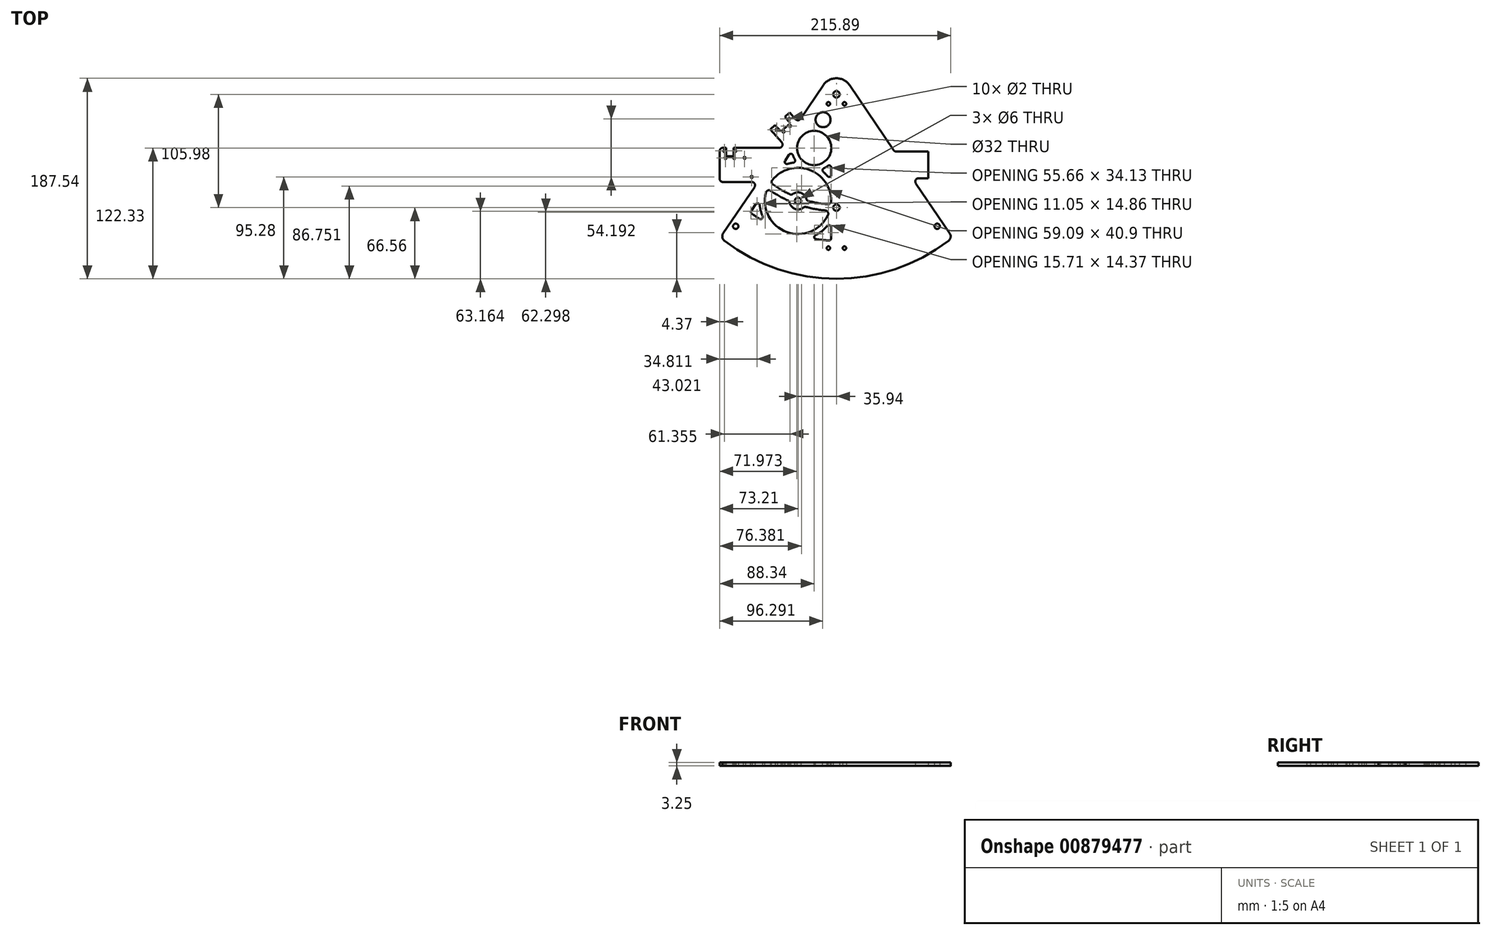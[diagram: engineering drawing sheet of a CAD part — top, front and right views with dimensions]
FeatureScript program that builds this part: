
annotation { "Feature Type Name" : "Feature", "Feature Type Description" : "" }
export const myFeature = defineFeature(function(context is Context, id is Id, definition is map)
    precondition{}
    {
        {
            var Q0;
            Q0=qCreatedBy(makeId("Top.planeOp"),FACE);
            var sketch = newSketch(context, id + "F0", { "sketchPlane" : qUnion([Q0])});
            skLineSegment(sketch, "E0", {"start": v(-12.44, 8.39) * mm, "end": v(-33.57, -22.95) * mm});
            skLineSegment(sketch, "E1", {"start": v(12.44, 8.39) * mm, "end": v(53.3, -52.2) * mm});
            skArc(sketch, "E2", {"start": v(-104.78, -136.9) * mm, "mid": v(0, -172.54) * mm, "end": v(104.78, -136.9) * mm});
            skPoint(sketch, "E3.visualSharp", {"position": v(0, 26.82) * mm});
            skArc(sketch, "E3.filletArc", {"start": v(12.44, 8.39) * mm, "mid": v(0, 15) * mm, "end": v(-12.44, 8.39) * mm});
            skPoint(sketch, "E4.visualSharp", {"position": v(108.47, -134) * mm});
            skArc(sketch, "E4.filletArc", {"start": v(104.78, -136.9) * mm, "mid": v(106.67, -133.75) * mm, "end": v(105.88, -130.15) * mm});
            skPoint(sketch, "E5.visualSharp", {"position": v(-108.47, -134) * mm});
            skArc(sketch, "E5.filletArc", {"start": v(-105.88, -130.15) * mm, "mid": v(-106.67, -133.75) * mm, "end": v(-104.78, -136.9) * mm});
            skLineSegment(sketch, "E6", {"start": v(-114.15, -172.54) * mm, "end": v(114.15, -172.54) * mm, "construction": true});
            skLineSegment(sketch, "E7", {"start": v(-114.15, 15) * mm, "end": v(114.15, 15) * mm, "construction": true});
            skPoint(sketch, "E8", {"position": v(-94.16, -123.45) * mm});
            skPoint(sketch, "E9", {"position": v(94.16, -123.45) * mm});
            skPoint(sketch, "E10", {"position": v(-7.5, -8.89) * mm});
            skPoint(sketch, "E11", {"position": v(7.5, -8.89) * mm});
            skLineSegment(sketch, "E12.bottom", {"start": v(55.79, -53.52) * mm, "end": v(85.7, -53.52) * mm});
            skLineSegment(sketch, "E12.top", {"start": v(76.7, -78.52) * mm, "end": v(85.7, -78.52) * mm});
            skLineSegment(sketch, "E12.right", {"start": v(85.7, -53.52) * mm, "end": v(85.7, -78.52) * mm});
            skLineSegment(sketch, "E13.trimOffspring", {"start": v(74.21, -83.2) * mm, "end": v(105.88, -130.15) * mm});
            skLineSegment(sketch, "E14.bottom", {"start": v(-53.43, -50.02) * mm, "end": v(-96.15, -50.02) * mm});
            skLineSegment(sketch, "E14.top", {"start": v(-79.06, -82.02) * mm, "end": v(-106.15, -82.02) * mm});
            skLineSegment(sketch, "E14.right", {"start": v(-109.15, -53.02) * mm, "end": v(-109.15, -79.02) * mm});
            skLineSegment(sketch, "E15.trimOffspring", {"start": v(-76.57, -86.7) * mm, "end": v(-105.88, -130.15) * mm});
            skLineSegment(sketch, "E16.top", {"start": v(-103.15, -58.02) * mm, "end": v(-96.15, -58.02) * mm});
            skLineSegment(sketch, "E16.left", {"start": v(-103.15, -50.02) * mm, "end": v(-103.15, -58.02) * mm});
            skLineSegment(sketch, "E16.right", {"start": v(-96.15, -50.02) * mm, "end": v(-96.15, -58.02) * mm});
            skLineSegment(sketch, "E17", {"start": v(-51.16, -45.05) * mm, "end": v(-61.82, -32.8) * mm});
            skLineSegment(sketch, "E18", {"start": v(-61.82, -32.8) * mm, "end": v(-57.3, -28.86) * mm});
            skLineSegment(sketch, "E19", {"start": v(-57.3, -28.86) * mm, "end": v(-52.04, -34.9) * mm});
            skLineSegment(sketch, "E20", {"start": v(-52.04, -34.9) * mm, "end": v(-42.99, -27.02) * mm});
            skLineSegment(sketch, "E21", {"start": v(-42.99, -27.02) * mm, "end": v(-48.23, -20.99) * mm});
            skLineSegment(sketch, "E22", {"start": v(-48.23, -20.99) * mm, "end": v(-43.7, -17.05) * mm});
            skLineSegment(sketch, "E23", {"start": v(-43.7, -17.05) * mm, "end": v(-38.32, -23.24) * mm});
            skLineSegment(sketch, "E24.trimOffspring", {"start": v(-103.15, -50.02) * mm, "end": v(-106.15, -50.02) * mm});
            skLineSegment(sketch, "E25", {"start": v(-114.15, 15) * mm, "end": v(-114.15, -172.54) * mm, "construction": true});
            skLineSegment(sketch, "E26", {"start": v(114.15, -172.54) * mm, "end": v(114.15, 15) * mm, "construction": true});
            skArc(sketch, "E27.filletArc", {"start": v(-53.43, -50.02) * mm, "mid": v(-50.7, -48.26) * mm, "end": v(-51.16, -45.05) * mm});
            skLineSegment(sketch, "E28", {"start": v(-48.23, -20.99) * mm, "end": v(-32.25, -20.99) * mm, "construction": true});
            skPoint(sketch, "E29.visualSharp", {"position": v(-35.76, -26.2) * mm});
            skArc(sketch, "E29.filletArc", {"start": v(-38.32, -23.24) * mm, "mid": v(-35.88, -24.27) * mm, "end": v(-33.57, -22.95) * mm});
            skPoint(sketch, "E30.visualSharp", {"position": v(-73.42, -82.02) * mm});
            skArc(sketch, "E30.filletArc", {"start": v(-76.57, -86.7) * mm, "mid": v(-76.4, -83.61) * mm, "end": v(-79.06, -82.02) * mm});
            skPoint(sketch, "E31.visualSharp", {"position": v(-109.15, -50.02) * mm});
            skArc(sketch, "E31.filletArc", {"start": v(-106.15, -50.02) * mm, "mid": v(-108.27, -50.9) * mm, "end": v(-109.15, -53.02) * mm});
            skPoint(sketch, "E32.visualSharp", {"position": v(-109.15, -82.02) * mm});
            skArc(sketch, "E32.filletArc", {"start": v(-109.15, -79.02) * mm, "mid": v(-108.27, -81.14) * mm, "end": v(-106.15, -82.02) * mm});
            skPoint(sketch, "E33.visualSharp", {"position": v(71.06, -78.52) * mm});
            skArc(sketch, "E33.filletArc", {"start": v(76.7, -78.52) * mm, "mid": v(74.05, -80.11) * mm, "end": v(74.21, -83.2) * mm});
            skPoint(sketch, "E34.visualSharp", {"position": v(54.2, -53.52) * mm});
            skArc(sketch, "E34.filletArc", {"start": v(53.3, -52.2) * mm, "mid": v(54.38, -53.17) * mm, "end": v(55.79, -53.52) * mm});
            skPoint(sketch, "E35", {"position": v(-7.5, -143.86) * mm});
            skPoint(sketch, "E36", {"position": v(7.5, -143.86) * mm});
            skPoint(sketch, "E37", {"position": v(0, -105.98) * mm});
            skSolve(sketch);
        }
        {
            var Q0;
            Q0=makeQuery(id+"F0.imprint","IMPRINT",FACE,{"disambiguationData":[TD([[makeQuery(id+"F0.imprint","IMPRINT",EDGE,{"derivedFrom":sQuery(id+"F0.wireOp",EDGE,"E0")}),1.0]])]});
            extrude(context, id + "F1", {"entities" : qUnion([Q0]), "depth" : 3.25 * mm, "offsetDistance" : 25 * mm});
        }
        {
            var Q0;
            Q0=sQuery(id+"F0.wireOp",VERTEX,"E9");
            var Q1;
            Q1=sQuery(id+"F0.wireOp",VERTEX,"E8");
            var Q2;
            Q2=makeQuery(id+"F1.opExtrude","SWEPT_BODY",BODY,{"disambiguationData":[OSD([sQuery(id+"F0.wireOp",EDGE,"E0"),sQuery(id+"F0.wireOp",EDGE,"E1"),sQuery(id+"F0.wireOp",EDGE,"E2"),sQuery(id+"F0.wireOp",EDGE,"E3.filletArc"),sQuery(id+"F0.wireOp",EDGE,"E4.filletArc"),sQuery(id+"F0.wireOp",EDGE,"E5.filletArc"),sQuery(id+"F0.wireOp",EDGE,"E12.bottom"),sQuery(id+"F0.wireOp",EDGE,"E12.top"),sQuery(id+"F0.wireOp",EDGE,"E12.right"),sQuery(id+"F0.wireOp",EDGE,"E13.trimOffspring"),sQuery(id+"F0.wireOp",EDGE,"E14.bottom"),sQuery(id+"F0.wireOp",EDGE,"E14.top"),sQuery(id+"F0.wireOp",EDGE,"E14.right"),sQuery(id+"F0.wireOp",EDGE,"E15.trimOffspring"),sQuery(id+"F0.wireOp",EDGE,"E16.top"),sQuery(id+"F0.wireOp",EDGE,"E16.left"),sQuery(id+"F0.wireOp",EDGE,"E16.right"),sQuery(id+"F0.wireOp",EDGE,"E17"),sQuery(id+"F0.wireOp",EDGE,"E18"),sQuery(id+"F0.wireOp",EDGE,"E19"),sQuery(id+"F0.wireOp",EDGE,"E20"),sQuery(id+"F0.wireOp",EDGE,"E21"),sQuery(id+"F0.wireOp",EDGE,"E22"),sQuery(id+"F0.wireOp",EDGE,"E23"),sQuery(id+"F0.wireOp",EDGE,"E24.trimOffspring"),sQuery(id+"F0.wireOp",EDGE,"E27.filletArc"),sQuery(id+"F0.wireOp",EDGE,"E29.filletArc"),sQuery(id+"F0.wireOp",EDGE,"E30.filletArc"),sQuery(id+"F0.wireOp",EDGE,"E31.filletArc"),sQuery(id+"F0.wireOp",EDGE,"E32.filletArc"),sQuery(id+"F0.wireOp",EDGE,"E33.filletArc"),sQuery(id+"F0.wireOp",EDGE,"E34.filletArc")])]});
            hole(context, id + "F2", {"style" : HoleStyle.SIMPLE, "endStyle" : HoleEndStyle.THROUGH, "oppositeDirection" : true, "standardTappedOrClearance" : lookupTablePath({ "standard" : "ISO", "engagement" : "75%", "pitch" : "1 mm", "size" : "M6", "type" : "Tapped" }), "standardBlindInLast" : lookupTablePath({ "standard" : "ISO", "engagement" : "75%", "pitch" : "1 mm", "size" : "M6", "type" : "Tapped" }), "holeDiameter" : 5 * mm, "majorDiameter" : 6 * mm, "showTappedDepth" : true, "isTappedThrough" : true, "tappedDepth" : 12 * mm, "tapClearance" : 3, "startFromSketch" : true, "locations" : qUnion([Q0, Q1]), "scope" : qUnion([Q2])});
        }
        {
            var Q0;
            Q0=sQuery(id+"F0.wireOp",VERTEX,"E10");
            var Q1;
            Q1=sQuery(id+"F0.wireOp",VERTEX,"E11");
            var Q2;
            Q2=sQuery(id+"F0.wireOp",VERTEX,"E35");
            var Q3;
            Q3=sQuery(id+"F0.wireOp",VERTEX,"E36");
            var Q4;
            Q4=makeQuery(id+"F1.opExtrude","SWEPT_BODY",BODY,{"disambiguationData":[OSD([sQuery(id+"F0.wireOp",EDGE,"E0"),sQuery(id+"F0.wireOp",EDGE,"E1"),sQuery(id+"F0.wireOp",EDGE,"E2"),sQuery(id+"F0.wireOp",EDGE,"E3.filletArc"),sQuery(id+"F0.wireOp",EDGE,"E4.filletArc"),sQuery(id+"F0.wireOp",EDGE,"E5.filletArc"),sQuery(id+"F0.wireOp",EDGE,"E12.bottom"),sQuery(id+"F0.wireOp",EDGE,"E12.top"),sQuery(id+"F0.wireOp",EDGE,"E12.right"),sQuery(id+"F0.wireOp",EDGE,"E13.trimOffspring"),sQuery(id+"F0.wireOp",EDGE,"E14.bottom"),sQuery(id+"F0.wireOp",EDGE,"E14.top"),sQuery(id+"F0.wireOp",EDGE,"E14.right"),sQuery(id+"F0.wireOp",EDGE,"E15.trimOffspring"),sQuery(id+"F0.wireOp",EDGE,"E16.top"),sQuery(id+"F0.wireOp",EDGE,"E16.left"),sQuery(id+"F0.wireOp",EDGE,"E16.right"),sQuery(id+"F0.wireOp",EDGE,"E17"),sQuery(id+"F0.wireOp",EDGE,"E18"),sQuery(id+"F0.wireOp",EDGE,"E19"),sQuery(id+"F0.wireOp",EDGE,"E20"),sQuery(id+"F0.wireOp",EDGE,"E21"),sQuery(id+"F0.wireOp",EDGE,"E22"),sQuery(id+"F0.wireOp",EDGE,"E23"),sQuery(id+"F0.wireOp",EDGE,"E24.trimOffspring"),sQuery(id+"F0.wireOp",EDGE,"E27.filletArc"),sQuery(id+"F0.wireOp",EDGE,"E29.filletArc"),sQuery(id+"F0.wireOp",EDGE,"E30.filletArc"),sQuery(id+"F0.wireOp",EDGE,"E31.filletArc"),sQuery(id+"F0.wireOp",EDGE,"E32.filletArc"),sQuery(id+"F0.wireOp",EDGE,"E33.filletArc"),sQuery(id+"F0.wireOp",EDGE,"E34.filletArc")])]});
            hole(context, id + "F3", {"style" : HoleStyle.SIMPLE, "endStyle" : HoleEndStyle.THROUGH, "oppositeDirection" : true, "standardTappedOrClearance" : lookupTablePath({ "standard" : "ISO", "engagement" : "75%", "pitch" : "0.7 mm", "size" : "M4", "type" : "Tapped" }), "standardBlindInLast" : lookupTablePath({ "standard" : "ISO", "engagement" : "75%", "pitch" : "0.7 mm", "size" : "M4", "type" : "Tapped" }), "holeDiameter" : 3.3 * mm, "majorDiameter" : 4 * mm, "showTappedDepth" : true, "isTappedThrough" : true, "tappedDepth" : 12 * mm, "tapClearance" : 3, "startFromSketch" : true, "locations" : qUnion([Q0, Q1, Q2, Q3]), "scope" : qUnion([Q4])});
        }
        {
            var Q0;
            Q0=sQuery(id+"F0.wireOp",VERTEX,"E3.filletArc.center");
            var Q1;
            Q1=sQuery(id+"F0.wireOp",VERTEX,"E37");
            var Q2;
            Q2=makeQuery(id+"F1.opExtrude","SWEPT_BODY",BODY,{"disambiguationData":[OSD([sQuery(id+"F0.wireOp",EDGE,"E0"),sQuery(id+"F0.wireOp",EDGE,"E1"),sQuery(id+"F0.wireOp",EDGE,"E2"),sQuery(id+"F0.wireOp",EDGE,"E3.filletArc"),sQuery(id+"F0.wireOp",EDGE,"E4.filletArc"),sQuery(id+"F0.wireOp",EDGE,"E5.filletArc"),sQuery(id+"F0.wireOp",EDGE,"E12.bottom"),sQuery(id+"F0.wireOp",EDGE,"E12.top"),sQuery(id+"F0.wireOp",EDGE,"E12.right"),sQuery(id+"F0.wireOp",EDGE,"E13.trimOffspring"),sQuery(id+"F0.wireOp",EDGE,"E14.bottom"),sQuery(id+"F0.wireOp",EDGE,"E14.top"),sQuery(id+"F0.wireOp",EDGE,"E14.right"),sQuery(id+"F0.wireOp",EDGE,"E15.trimOffspring"),sQuery(id+"F0.wireOp",EDGE,"E16.top"),sQuery(id+"F0.wireOp",EDGE,"E16.left"),sQuery(id+"F0.wireOp",EDGE,"E16.right"),sQuery(id+"F0.wireOp",EDGE,"E17"),sQuery(id+"F0.wireOp",EDGE,"E18"),sQuery(id+"F0.wireOp",EDGE,"E19"),sQuery(id+"F0.wireOp",EDGE,"E20"),sQuery(id+"F0.wireOp",EDGE,"E21"),sQuery(id+"F0.wireOp",EDGE,"E22"),sQuery(id+"F0.wireOp",EDGE,"E23"),sQuery(id+"F0.wireOp",EDGE,"E24.trimOffspring"),sQuery(id+"F0.wireOp",EDGE,"E27.filletArc"),sQuery(id+"F0.wireOp",EDGE,"E29.filletArc"),sQuery(id+"F0.wireOp",EDGE,"E30.filletArc"),sQuery(id+"F0.wireOp",EDGE,"E31.filletArc"),sQuery(id+"F0.wireOp",EDGE,"E32.filletArc"),sQuery(id+"F0.wireOp",EDGE,"E33.filletArc"),sQuery(id+"F0.wireOp",EDGE,"E34.filletArc")])]});
            hole(context, id + "F4", {"style" : HoleStyle.SIMPLE, "endStyle" : HoleEndStyle.THROUGH, "oppositeDirection" : true, "standardTappedOrClearance" : lookupTablePath({ "standard" : "ISO", "size" : "6", "type" : "Drilled" }), "standardBlindInLast" : lookupTablePath({ "standard" : "ISO", "size" : "6", "type" : "Drilled" }), "holeDiameter" : 6 * mm, "majorDiameter" : 4 * mm, "isTappedThrough" : true, "tappedDepth" : 12 * mm, "tapClearance" : 3, "startFromSketch" : true, "locations" : qUnion([Q0, Q1]), "scope" : qUnion([Q2])});
        }
        {
            var Q0;
            Q0=makeQuery(id+"F1.opExtrude","CAP_FACE",FACE,{"disambiguationData":[OSD([sQuery(id+"F0.wireOp",EDGE,"E0"),sQuery(id+"F0.wireOp",EDGE,"E1"),sQuery(id+"F0.wireOp",EDGE,"E2"),sQuery(id+"F0.wireOp",EDGE,"E3.filletArc"),sQuery(id+"F0.wireOp",EDGE,"E4.filletArc"),sQuery(id+"F0.wireOp",EDGE,"E5.filletArc"),sQuery(id+"F0.wireOp",EDGE,"E12.bottom"),sQuery(id+"F0.wireOp",EDGE,"E12.top"),sQuery(id+"F0.wireOp",EDGE,"E12.right"),sQuery(id+"F0.wireOp",EDGE,"E13.trimOffspring"),sQuery(id+"F0.wireOp",EDGE,"E14.bottom"),sQuery(id+"F0.wireOp",EDGE,"E14.top"),sQuery(id+"F0.wireOp",EDGE,"E14.right"),sQuery(id+"F0.wireOp",EDGE,"E15.trimOffspring"),sQuery(id+"F0.wireOp",EDGE,"E16.top"),sQuery(id+"F0.wireOp",EDGE,"E16.left"),sQuery(id+"F0.wireOp",EDGE,"E16.right"),sQuery(id+"F0.wireOp",EDGE,"E17"),sQuery(id+"F0.wireOp",EDGE,"E18"),sQuery(id+"F0.wireOp",EDGE,"E19"),sQuery(id+"F0.wireOp",EDGE,"E20"),sQuery(id+"F0.wireOp",EDGE,"E21"),sQuery(id+"F0.wireOp",EDGE,"E22"),sQuery(id+"F0.wireOp",EDGE,"E23"),sQuery(id+"F0.wireOp",EDGE,"E24.trimOffspring"),sQuery(id+"F0.wireOp",EDGE,"E27.filletArc"),sQuery(id+"F0.wireOp",EDGE,"E29.filletArc"),sQuery(id+"F0.wireOp",EDGE,"E30.filletArc"),sQuery(id+"F0.wireOp",EDGE,"E31.filletArc"),sQuery(id+"F0.wireOp",EDGE,"E32.filletArc"),sQuery(id+"F0.wireOp",EDGE,"E33.filletArc"),sQuery(id+"F0.wireOp",EDGE,"E34.filletArc")])],"isStart":false});
            var sketch = newSketch(context, id + "F5", { "sketchPlane" : qUnion([Q0])});
            skPoint(sketch, "E38", {"position": v(-55.78, -33.07) * mm});
            skPoint(sketch, "E39", {"position": v(-49.46, -34.81) * mm});
            skPoint(sketch, "E40", {"position": v(-43.43, -29.57) * mm});
            skPoint(sketch, "E41", {"position": v(-44.27, -23.07) * mm});
            skPoint(sketch, "E42", {"position": v(-104.78, -53.02) * mm});
            skPoint(sketch, "E43", {"position": v(-94.53, -53.02) * mm});
            skPoint(sketch, "E44", {"position": v(-103.65, -59.46) * mm});
            skPoint(sketch, "E45", {"position": v(-95.65, -59.46) * mm});
            skPoint(sketch, "E46", {"position": v(-85.83, -59.46) * mm});
            skPoint(sketch, "E47", {"position": v(-79.2, -77.26) * mm});
            skLineSegment(sketch, "E48", {"start": v(-49.46, -34.81) * mm, "end": v(-43.43, -29.57) * mm, "construction": true});
            skLineSegment(sketch, "E49", {"start": v(-55.78, -33.07) * mm, "end": v(-44.27, -23.07) * mm, "construction": true});
            skLineSegment(sketch, "E50", {"start": v(-47.51, -30.96) * mm, "end": v(-52.76, -24.92) * mm, "construction": true});
            skLineSegment(sketch, "E51", {"start": v(-57.3, -28.86) * mm, "end": v(-48.23, -20.99) * mm, "construction": true});
            skLineSegment(sketch, "E52", {"start": v(-99.65, -58.02) * mm, "end": v(-99.65, -50.02) * mm, "construction": true});
            skSolve(sketch);
        }
        {
            var Q0;
            Q0=sQuery(id+"F5.wireOp",VERTEX,"E46");
            var Q1;
            Q1=sQuery(id+"F5.wireOp",VERTEX,"E47");
            var Q2;
            Q2=sQuery(id+"F5.wireOp",VERTEX,"E45");
            var Q3;
            Q3=sQuery(id+"F5.wireOp",VERTEX,"E43");
            var Q4;
            Q4=sQuery(id+"F5.wireOp",VERTEX,"E44");
            var Q5;
            Q5=sQuery(id+"F5.wireOp",VERTEX,"E42");
            var Q6;
            Q6=sQuery(id+"F5.wireOp",VERTEX,"E39");
            var Q7;
            Q7=sQuery(id+"F5.wireOp",VERTEX,"E40");
            var Q8;
            Q8=sQuery(id+"F0.wireOp",VERTEX,"E29.visualSharp");
            var Q9;
            Q9=sQuery(id+"F5.wireOp",VERTEX,"E41");
            var Q10;
            Q10=sQuery(id+"F5.wireOp",VERTEX,"E38");
            var Q11;
            Q11=makeQuery(id+"F1.opExtrude","SWEPT_BODY",BODY,{"disambiguationData":[OSD([sQuery(id+"F0.wireOp",EDGE,"E0"),sQuery(id+"F0.wireOp",EDGE,"E1"),sQuery(id+"F0.wireOp",EDGE,"E2"),sQuery(id+"F0.wireOp",EDGE,"E3.filletArc"),sQuery(id+"F0.wireOp",EDGE,"E4.filletArc"),sQuery(id+"F0.wireOp",EDGE,"E5.filletArc"),sQuery(id+"F0.wireOp",EDGE,"E12.bottom"),sQuery(id+"F0.wireOp",EDGE,"E12.top"),sQuery(id+"F0.wireOp",EDGE,"E12.right"),sQuery(id+"F0.wireOp",EDGE,"E13.trimOffspring"),sQuery(id+"F0.wireOp",EDGE,"E14.bottom"),sQuery(id+"F0.wireOp",EDGE,"E14.top"),sQuery(id+"F0.wireOp",EDGE,"E14.right"),sQuery(id+"F0.wireOp",EDGE,"E15.trimOffspring"),sQuery(id+"F0.wireOp",EDGE,"E16.top"),sQuery(id+"F0.wireOp",EDGE,"E16.left"),sQuery(id+"F0.wireOp",EDGE,"E16.right"),sQuery(id+"F0.wireOp",EDGE,"E17"),sQuery(id+"F0.wireOp",EDGE,"E18"),sQuery(id+"F0.wireOp",EDGE,"E19"),sQuery(id+"F0.wireOp",EDGE,"E20"),sQuery(id+"F0.wireOp",EDGE,"E21"),sQuery(id+"F0.wireOp",EDGE,"E22"),sQuery(id+"F0.wireOp",EDGE,"E23"),sQuery(id+"F0.wireOp",EDGE,"E24.trimOffspring"),sQuery(id+"F0.wireOp",EDGE,"E27.filletArc"),sQuery(id+"F0.wireOp",EDGE,"E29.filletArc"),sQuery(id+"F0.wireOp",EDGE,"E30.filletArc"),sQuery(id+"F0.wireOp",EDGE,"E31.filletArc"),sQuery(id+"F0.wireOp",EDGE,"E32.filletArc"),sQuery(id+"F0.wireOp",EDGE,"E33.filletArc"),sQuery(id+"F0.wireOp",EDGE,"E34.filletArc")])]});
            hole(context, id + "F6", {"style" : HoleStyle.SIMPLE, "endStyle" : HoleEndStyle.THROUGH, "standardTappedOrClearance" : lookupTablePath({ "standard" : "ISO", "size" : "2", "type" : "Drilled" }), "standardBlindInLast" : lookupTablePath({ "standard" : "ISO", "size" : "2", "type" : "Drilled" }), "holeDiameter" : 2 * mm, "majorDiameter" : 4 * mm, "isTappedThrough" : true, "tappedDepth" : 12 * mm, "tapClearance" : 3, "startFromSketch" : true, "locations" : qUnion([Q0, Q1, Q2, Q3, Q4, Q5, Q6, Q7, Q8, Q9, Q10]), "scope" : qUnion([Q11])});
        }
        {
            var Q0;
            Q0=makeQuery(id+"F1.opExtrude","CAP_FACE",FACE,{"disambiguationData":[OSD([sQuery(id+"F0.wireOp",EDGE,"E0"),sQuery(id+"F0.wireOp",EDGE,"E1"),sQuery(id+"F0.wireOp",EDGE,"E2"),sQuery(id+"F0.wireOp",EDGE,"E3.filletArc"),sQuery(id+"F0.wireOp",EDGE,"E4.filletArc"),sQuery(id+"F0.wireOp",EDGE,"E5.filletArc"),sQuery(id+"F0.wireOp",EDGE,"E12.bottom"),sQuery(id+"F0.wireOp",EDGE,"E12.top"),sQuery(id+"F0.wireOp",EDGE,"E12.right"),sQuery(id+"F0.wireOp",EDGE,"E13.trimOffspring"),sQuery(id+"F0.wireOp",EDGE,"E14.bottom"),sQuery(id+"F0.wireOp",EDGE,"E14.top"),sQuery(id+"F0.wireOp",EDGE,"E14.right"),sQuery(id+"F0.wireOp",EDGE,"E15.trimOffspring"),sQuery(id+"F0.wireOp",EDGE,"E16.top"),sQuery(id+"F0.wireOp",EDGE,"E16.left"),sQuery(id+"F0.wireOp",EDGE,"E16.right"),sQuery(id+"F0.wireOp",EDGE,"E17"),sQuery(id+"F0.wireOp",EDGE,"E18"),sQuery(id+"F0.wireOp",EDGE,"E19"),sQuery(id+"F0.wireOp",EDGE,"E20"),sQuery(id+"F0.wireOp",EDGE,"E21"),sQuery(id+"F0.wireOp",EDGE,"E22"),sQuery(id+"F0.wireOp",EDGE,"E23"),sQuery(id+"F0.wireOp",EDGE,"E24.trimOffspring"),sQuery(id+"F0.wireOp",EDGE,"E27.filletArc"),sQuery(id+"F0.wireOp",EDGE,"E29.filletArc"),sQuery(id+"F0.wireOp",EDGE,"E30.filletArc"),sQuery(id+"F0.wireOp",EDGE,"E31.filletArc"),sQuery(id+"F0.wireOp",EDGE,"E32.filletArc"),sQuery(id+"F0.wireOp",EDGE,"E33.filletArc"),sQuery(id+"F0.wireOp",EDGE,"E34.filletArc")])],"isStart":false});
            var sketch = newSketch(context, id + "F7", { "sketchPlane" : qUnion([Q0])});
            skCircle(sketch, "E53", {"center": v(-12.53, -23.76) * mm, "radius": 7 * mm});
            skCircle(sketch, "E54", {"center": v(-20.8, -50.21) * mm, "radius": 16 * mm});
            skArc(sketch, "E55", {"start": v(-71.72, -103.72) * mm, "mid": v(-70.73, -108.97) * mm, "end": v(-68.97, -114.02) * mm});
            skCircle(sketch, "E56", {"center": v(-35.94, -99.7) * mm, "radius": 3 * mm});
            skArc(sketch, "E57", {"start": v(-65.98, -92.03) * mm, "mid": v(-46.45, -128.86) * mm, "end": v(-7.92, -112.96) * mm});
            skArc(sketch, "E58", {"start": v(-79.02, -111.78) * mm, "mid": v(-75.47, -114.2) * mm, "end": v(-71.86, -116.51) * mm});
            skLineSegment(sketch, "E59", {"start": v(-79.53, -109.03) * mm, "end": v(-75.36, -102.83) * mm});
            skArc(sketch, "E60", {"start": v(-40.7, -56.93) * mm, "mid": v(-39.89, -59) * mm, "end": v(-38.85, -60.96) * mm});
            skArc(sketch, "E61.trimOffspring", {"start": v(-40.32, -63.97) * mm, "mid": v(-43.08, -64.42) * mm, "end": v(-45.8, -65.08) * mm});
            skArc(sketch, "E62.trimOffspring", {"start": v(-8.4, -76.5) * mm, "mid": v(-10.29, -74.44) * mm, "end": v(-12.32, -72.53) * mm});
            skLineSegment(sketch, "E63.trimOffspring", {"start": v(-4.86, -68.5) * mm, "end": v(-4.88, -75.23) * mm});
            skArc(sketch, "E64.trimOffspring", {"start": v(-11.86, -69.2) * mm, "mid": v(-9.9, -68.16) * mm, "end": v(-8.07, -66.9) * mm});
            skArc(sketch, "E65.trimOffspring", {"start": v(-19.64, -131.8) * mm, "mid": v(-13.65, -127.97) * mm, "end": v(-8.53, -123.04) * mm});
            skLineSegment(sketch, "E66.trimOffspring", {"start": v(-5, -124.34) * mm, "end": v(-5.03, -134.71) * mm});
            skArc(sketch, "E67.trimOffspring", {"start": v(-19.01, -135.56) * mm, "mid": v(-13.09, -136.26) * mm, "end": v(-7.14, -136.7) * mm});
            skLineSegment(sketch, "E68.trimOffspring", {"start": v(-48, -62.04) * mm, "end": v(-44.26, -56.45) * mm});
            skPoint(sketch, "E69.visualSharp", {"position": v(-80.6, -110.64) * mm});
            skArc(sketch, "E69.filletArc", {"start": v(-79.53, -109.03) * mm, "mid": v(-79.83, -110.5) * mm, "end": v(-79.02, -111.78) * mm});
            skPoint(sketch, "E70.visualSharp", {"position": v(-65.55, -120.17) * mm});
            skArc(sketch, "E70.filletArc", {"start": v(-71.86, -116.51) * mm, "mid": v(-69.5, -116.32) * mm, "end": v(-68.97, -114.02) * mm});
            skPoint(sketch, "E71.visualSharp", {"position": v(-71.88, -97.63) * mm});
            skArc(sketch, "E71.filletArc", {"start": v(-71.72, -103.72) * mm, "mid": v(-73.23, -102) * mm, "end": v(-75.36, -102.83) * mm});
            skPoint(sketch, "E72.visualSharp", {"position": v(-26.2, -134.36) * mm});
            skArc(sketch, "E72.filletArc", {"start": v(-19.64, -131.8) * mm, "mid": v(-20.7, -133.91) * mm, "end": v(-19.01, -135.56) * mm});
            skLineSegment(sketch, "E73", {"start": v(-75.36, -102.83) * mm, "end": v(-51.5, -67.23) * mm, "construction": true});
            skLineSegment(sketch, "E74", {"start": v(-4.9, -81.48) * mm, "end": v(-4.99, -118.08) * mm, "construction": true});
            skLineSegment(sketch, "E75", {"start": v(-4.85, -63.85) * mm, "end": v(-4.67, 2.58) * mm, "construction": true});
            skLineSegment(sketch, "E76", {"start": v(-4.67, 2.58) * mm, "end": v(-41.67, -52.6) * mm, "construction": true});
            skPoint(sketch, "E77.visualSharp", {"position": v(-4.99, -118.08) * mm});
            skArc(sketch, "E77.filletArc", {"start": v(-5, -124.34) * mm, "mid": v(-6.31, -122.46) * mm, "end": v(-8.53, -123.04) * mm});
            skPoint(sketch, "E78.visualSharp", {"position": v(-5.04, -136.8) * mm});
            skArc(sketch, "E78.filletArc", {"start": v(-7.14, -136.7) * mm, "mid": v(-5.66, -136.16) * mm, "end": v(-5.03, -134.71) * mm});
            skPoint(sketch, "E79.visualSharp", {"position": v(-4.9, -81.48) * mm});
            skArc(sketch, "E79.filletArc", {"start": v(-8.4, -76.5) * mm, "mid": v(-6.2, -77.1) * mm, "end": v(-4.88, -75.23) * mm});
            skPoint(sketch, "E80.visualSharp", {"position": v(-15.03, -70.4) * mm});
            skArc(sketch, "E80.filletArc", {"start": v(-11.86, -69.2) * mm, "mid": v(-13, -70.74) * mm, "end": v(-12.32, -72.53) * mm});
            skPoint(sketch, "E81.visualSharp", {"position": v(-4.85, -63.85) * mm});
            skArc(sketch, "E81.filletArc", {"start": v(-4.86, -68.5) * mm, "mid": v(-5.97, -66.7) * mm, "end": v(-8.07, -66.9) * mm});
            skPoint(sketch, "E82.visualSharp", {"position": v(-51.5, -67.23) * mm});
            skArc(sketch, "E82.filletArc", {"start": v(-48, -62.04) * mm, "mid": v(-47.96, -64.33) * mm, "end": v(-45.8, -65.08) * mm});
            skPoint(sketch, "E83.visualSharp", {"position": v(-41.67, -52.6) * mm});
            skArc(sketch, "E83.filletArc", {"start": v(-40.7, -56.93) * mm, "mid": v(-42.34, -55.59) * mm, "end": v(-44.26, -56.45) * mm});
            skPoint(sketch, "E84.visualSharp", {"position": v(-36.9, -63.71) * mm});
            skArc(sketch, "E84.filletArc", {"start": v(-40.32, -63.97) * mm, "mid": v(-38.77, -62.86) * mm, "end": v(-38.85, -60.96) * mm});
            skArc(sketch, "E85", {"start": v(-43.76, -101.37) * mm, "mid": v(-38.65, -107.23) * mm, "end": v(-30.98, -105.98) * mm});
            skLineSegment(sketch, "E86", {"start": v(-35.94, -99.7) * mm, "end": v(-4.67, 2.58) * mm, "construction": true});
            skArc(sketch, "E87", {"start": v(-10.35, -108.69) * mm, "mid": v(-19.41, -107.44) * mm, "end": v(-28.34, -105.44) * mm});
            skArc(sketch, "E88", {"start": v(-26.05, -99.84) * mm, "mid": v(-17.18, -101.74) * mm, "end": v(-8.18, -102.86) * mm});
            skArc(sketch, "E89", {"start": v(-61.38, -90.3) * mm, "mid": v(-53.6, -95.12) * mm, "end": v(-45.45, -99.27) * mm});
            skArc(sketch, "E90", {"start": v(-59.33, -84.42) * mm, "mid": v(-51.69, -89.3) * mm, "end": v(-43.64, -93.5) * mm});
            skArc(sketch, "E91.trimOffspring", {"start": v(-28.2, -97.69) * mm, "mid": v(-33.23, -92.17) * mm, "end": v(-40.62, -93.21) * mm});
            skArc(sketch, "E92.trimOffspring", {"start": v(-4.94, -99.88) * mm, "mid": v(-25.43, -70.54) * mm, "end": v(-59.93, -80.06) * mm});
            skPoint(sketch, "E93.visualSharp", {"position": v(-61.8, -82.62) * mm});
            skArc(sketch, "E93.filletArc", {"start": v(-59.93, -80.06) * mm, "mid": v(-60.58, -82.37) * mm, "end": v(-59.33, -84.42) * mm});
            skPoint(sketch, "E94.visualSharp", {"position": v(-64.64, -87.99) * mm});
            skArc(sketch, "E94.filletArc", {"start": v(-61.38, -90.3) * mm, "mid": v(-64.13, -89.97) * mm, "end": v(-65.98, -92.03) * mm});
            skPoint(sketch, "E95.visualSharp", {"position": v(-6.37, -109) * mm});
            skArc(sketch, "E95.filletArc", {"start": v(-7.92, -112.96) * mm, "mid": v(-8.02, -110.2) * mm, "end": v(-10.35, -108.69) * mm});
            skPoint(sketch, "E96.visualSharp", {"position": v(-5.12, -103.05) * mm});
            skArc(sketch, "E96.filletArc", {"start": v(-8.18, -102.86) * mm, "mid": v(-5.91, -102.07) * mm, "end": v(-4.94, -99.88) * mm});
            skPoint(sketch, "E97.visualSharp", {"position": v(-27.95, -99.32) * mm});
            skArc(sketch, "E97.filletArc", {"start": v(-28.2, -97.69) * mm, "mid": v(-27.42, -99.05) * mm, "end": v(-26.05, -99.84) * mm});
            skPoint(sketch, "E98.visualSharp", {"position": v(-41.85, -94.31) * mm});
            skArc(sketch, "E98.filletArc", {"start": v(-43.64, -93.5) * mm, "mid": v(-42.1, -93.76) * mm, "end": v(-40.62, -93.21) * mm});
            skPoint(sketch, "E99.visualSharp", {"position": v(-43.94, -99.95) * mm});
            skArc(sketch, "E99.filletArc", {"start": v(-43.76, -101.37) * mm, "mid": v(-44.36, -100.12) * mm, "end": v(-45.45, -99.27) * mm});
            skPoint(sketch, "E100.visualSharp", {"position": v(-29.94, -105) * mm});
            skArc(sketch, "E100.filletArc", {"start": v(-28.34, -105.44) * mm, "mid": v(-29.73, -105.4) * mm, "end": v(-30.98, -105.98) * mm});
            skSolve(sketch);
        }
        {
            var Q0;
            Q0=makeQuery(id+"F7.imprint","IMPRINT",FACE,{"disambiguationData":[TD([[makeQuery(id+"F7.imprint","IMPRINT",EDGE,{"derivedFrom":sQuery(id+"F7.wireOp",EDGE,"E54")}),1.0]])]});
            var Q1;
            Q1=makeQuery(id+"F7.imprint","IMPRINT",FACE,{"disambiguationData":[TD([[makeQuery(id+"F7.imprint","IMPRINT",EDGE,{"derivedFrom":sQuery(id+"F7.wireOp",EDGE,"E53")}),1.0]])]});
            var Q2;
            Q2=makeQuery(id+"F7.imprint","IMPRINT",FACE,{"disambiguationData":[TD([[makeQuery(id+"F7.imprint","IMPRINT",EDGE,{"derivedFrom":sQuery(id+"F7.wireOp",EDGE,"E62.trimOffspring")}),-1.0]])]});
            var Q3;
            Q3=makeQuery(id+"F7.imprint","IMPRINT",FACE,{"disambiguationData":[TD([[makeQuery(id+"F7.imprint","IMPRINT",EDGE,{"derivedFrom":sQuery(id+"F7.wireOp",EDGE,"E60")}),-1.0]])]});
            var Q4;
            Q4=makeQuery(id+"F7.imprint","IMPRINT",FACE,{"disambiguationData":[TD([[makeQuery(id+"F7.imprint","IMPRINT",EDGE,{"derivedFrom":sQuery(id+"F7.wireOp",EDGE,"E88")}),1.0]])]});
            var Q5;
            Q5=makeQuery(id+"F7.imprint","IMPRINT",FACE,{"disambiguationData":[TD([[makeQuery(id+"F7.imprint","IMPRINT",EDGE,{"derivedFrom":sQuery(id+"F7.wireOp",EDGE,"E56")}),1.0]])]});
            var Q6;
            Q6=makeQuery(id+"F7.imprint","IMPRINT",FACE,{"disambiguationData":[TD([[makeQuery(id+"F7.imprint","IMPRINT",EDGE,{"derivedFrom":sQuery(id+"F7.wireOp",EDGE,"E57")}),1.0]])]});
            var Q7;
            Q7=makeQuery(id+"F7.imprint","IMPRINT",FACE,{"disambiguationData":[TD([[makeQuery(id+"F7.imprint","IMPRINT",EDGE,{"derivedFrom":sQuery(id+"F7.wireOp",EDGE,"E55")}),-1.0]])]});
            var Q8;
            Q8=makeQuery(id+"F7.imprint","IMPRINT",FACE,{"disambiguationData":[TD([[makeQuery(id+"F7.imprint","IMPRINT",EDGE,{"derivedFrom":sQuery(id+"F7.wireOp",EDGE,"E65.trimOffspring")}),-1.0]])]});
            extrude(context, id + "F8", {"entities" : qUnion([Q0, Q1, Q2, Q3, Q4, Q5, Q6, Q7, Q8]), "operationType" : NewBodyOperationType.REMOVE, "endBound" : BoundingType.THROUGH_ALL, "oppositeDirection" : true, "depth" : 25 * mm, "offsetDistance" : 25 * mm});
        }
    });
